# Revit family: Indoor_Pendant Lamp_Santa&Cole_Vaso
name_source: partatom
category: Luminarias
revit_build: Autodesk Revit 2018 (Build: 20170223_1515(x64)
units: mm (PartAtom-declared; Revit-internal decimal feet)

## family parameters
Anfitrión = Cara
Compartido = No
Corte con vacíos al cargar = No
Cota de conector redondo = Diámetro de uso
Origen de luz = Sí
Punto de cálculo de habitación = No
Tipo de pieza = Normal

## types (3) — shared parameters
Archivo de red fotométrica = VASPA0X (CL004A22F001G).IES
Assembly Instructions - CE = https://www.santacole.com
Assembly Instructions - UL = https://www.santacole.com
Cambio de temperatura de color de luz atenuada = <Ninguno>
Carga aparente = 12 W
Elevación por defecto = 1219 mm
Fabricante = Santa & Cole
Filtro de color = 16777215
Load = 12 W
Manufacturer website = http://www.santacole.com
Modelo = Vaso
Technical Information = https://www.santacole.com
URL = https://www.santacole.com
Voltaje (90-305 V) = 220 V
Ángulo de inclinación = -90.00°

## per-type parameters (varying)
| type | Code | Material |
| Vaso - Aluminium Grey | VASPA03X | Santa & Cole - Grey Aluminium |
| Vaso - Black | VASPA02X | Santa & Cole - Black Matte Finish |
| Vaso - White | VASPA01X | Santa & Cole - White Matte Finish |

## geometry (parser evidence)
native form markers: Sweep x2
no freeform markers — native parametric forms only
